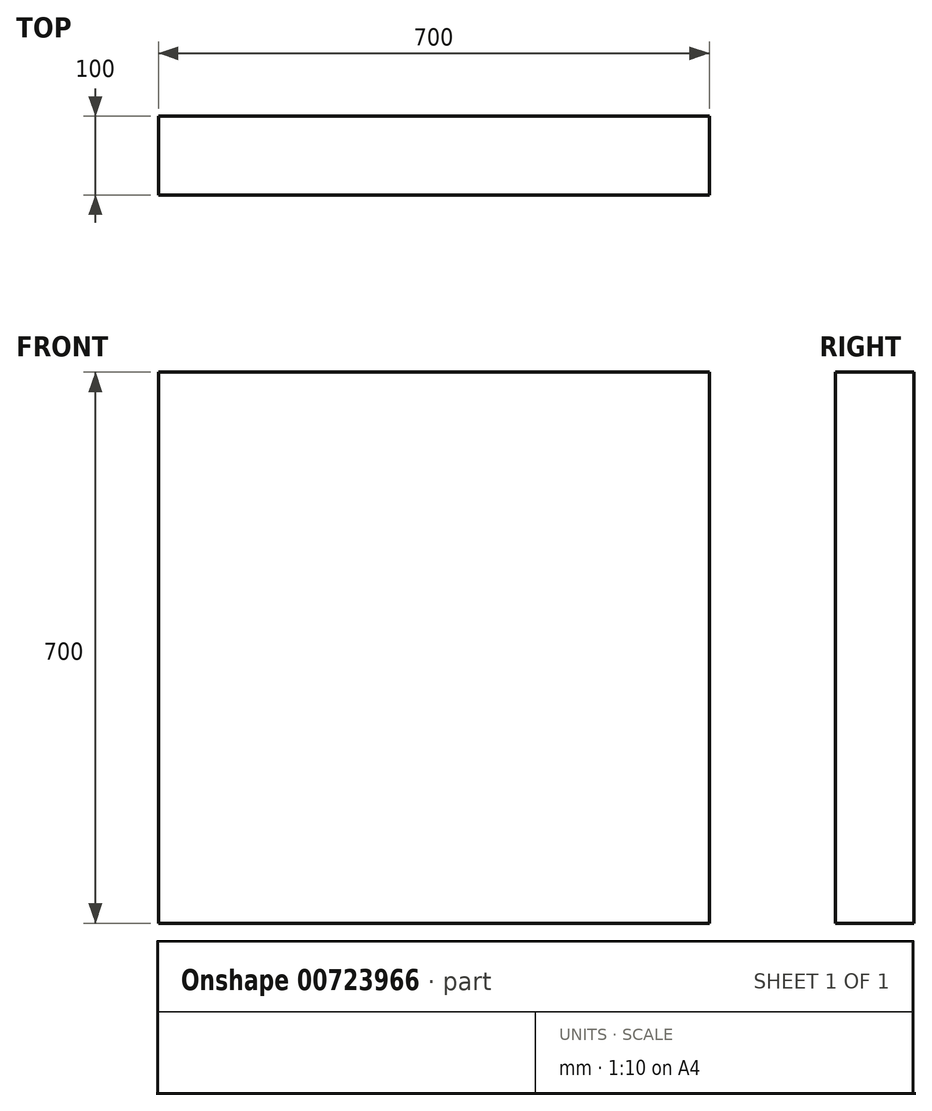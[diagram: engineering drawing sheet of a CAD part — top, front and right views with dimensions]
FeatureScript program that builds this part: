
annotation { "Feature Type Name" : "Feature", "Feature Type Description" : "" }
export const myFeature = defineFeature(function(context is Context, id is Id, definition is map)
    precondition{}
    {
        {
            var Q0;
            Q0=qCreatedBy(makeId("Front.planeOp"),FACE);
            var sketch = newSketch(context, id + "F0", { "sketchPlane" : qUnion([Q0])});
            skLineSegment(sketch, "E0.bottom", {"start": v(-631.3, 666.72) * mm, "end": v(68.7, 666.72) * mm});
            skLineSegment(sketch, "E0.top", {"start": v(-631.3, -33.28) * mm, "end": v(68.7, -33.28) * mm});
            skLineSegment(sketch, "E0.left", {"start": v(-631.3, 666.72) * mm, "end": v(-631.3, -33.28) * mm});
            skLineSegment(sketch, "E0.right", {"start": v(68.7, 666.72) * mm, "end": v(68.7, -33.28) * mm});
            skSolve(sketch);
        }
        {
            var Q0;
            Q0 = qSketchRegion(id + "F0", true);
            extrude(context, id + "F1", {"entities" : qUnion([Q0]), "depth" : 100 * mm, "offsetDistance" : 25 * mm});
        }
    });
